# Revit family: EB-705_Ciclon LS
name_source: partatom
category: Aparatos sanitarios
revit_build: Autodesk Revit 2015 (Build: 20140606_1530(x64)
units: mm (PartAtom-declared; Revit-internal decimal feet)

## types (1)
- EB-705 CICLON LS
    Altura = 278 mm
    Altura máx. de bombeo = 7 m vertical
    Carga aparente = 200 VA
    Caudal = 2.5 L/s
    Certificados = http://www.jimten.com
    Clasificación de cargas = Aparato eléctrico - Unidad de vivienda
    Comentarios de tipo = FACIL MANTENIMIENTO GRACIAS A SU SISTEMA CASET. SILENCIOSO.
    Descripción = ESTACION DE BOMBEO ELECTRODOMESTICOS
    Diámetro Impulsión = 32 mm  [stored 0.104987 ft]
    Diámetro Toma Lateral = 40 mm  [stored 0.131234 ft]
    Diámetro Toma Superior = 40 mm  [stored 0.131234 ft]
    Electricidad = 220-240 VAC 50HZ
    Electrodomésticos = Sí
    Entradas = 5 x Ø40 mm
    Fabricante = Jimten
    Material = Polipropileno (Blanco)
    Modelo = EB-705 CICLON LS
    Número de polos = 1
    Potencia = 390 W
    Profundidad = 180 mm  [stored 0.590551 ft]
    Referencia = 75401
    Salida = 1 x Ø32mm
    URL = http://www.jimten.com
    Ud.Desagüe Bidé-Ducha = 2
    Ud.Desagüe Lavabo = 1
    Voltaje = 230 V
    WC = No

note: [stored X ft] marks values corroborated as IEEE doubles in the binary element streams (Revit-internal decimal feet)

## geometry (parser evidence)
native form markers: Blend x3, Sweep x2
no freeform markers — native parametric forms only
